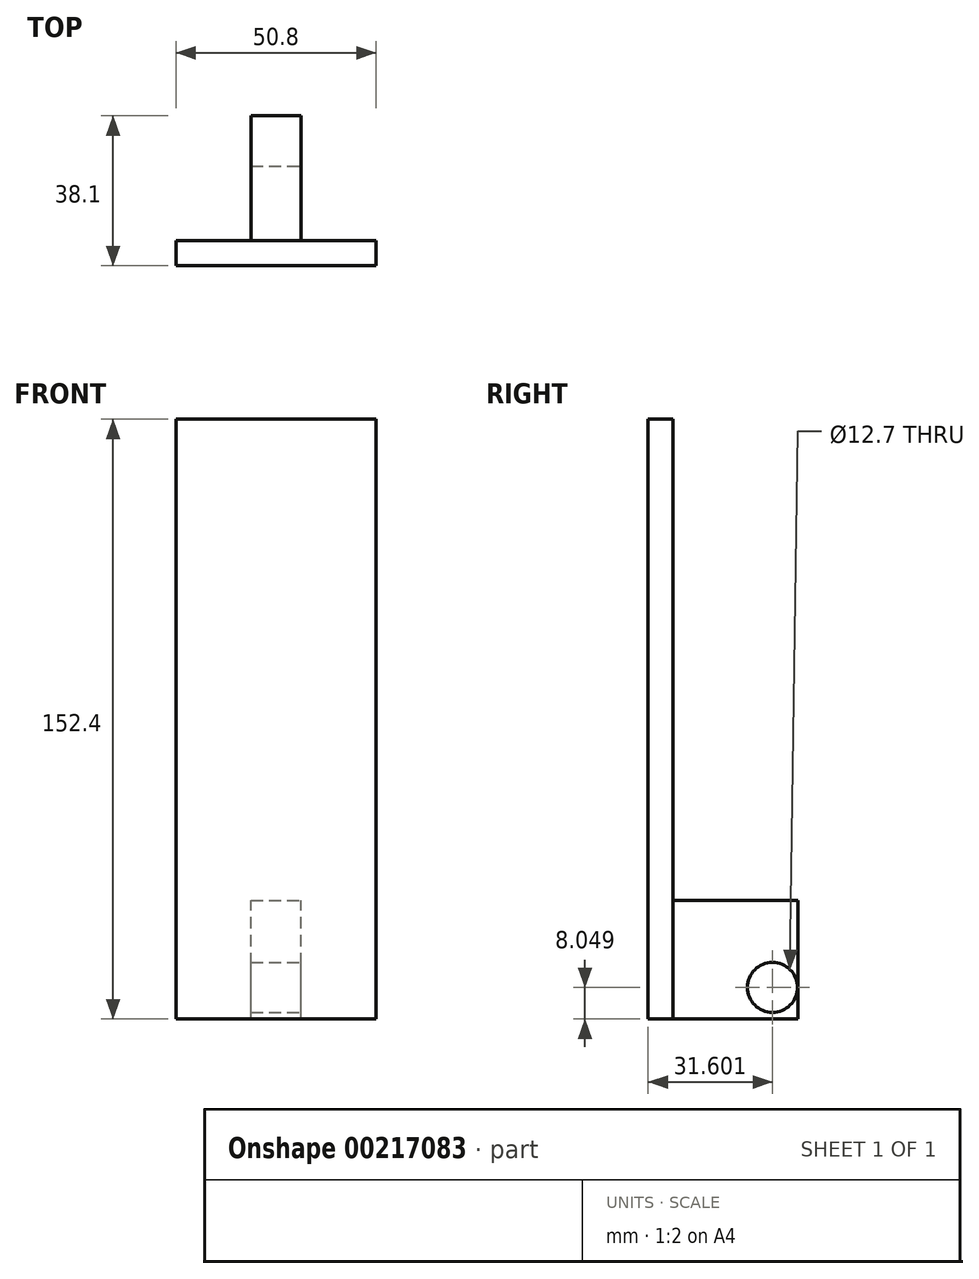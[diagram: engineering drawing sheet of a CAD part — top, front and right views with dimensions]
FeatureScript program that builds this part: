
annotation { "Feature Type Name" : "Feature", "Feature Type Description" : "" }
export const myFeature = defineFeature(function(context is Context, id is Id, definition is map)
    precondition{}
    {
        {
            var Q0;
            Q0=qCreatedBy(makeId("Front.planeOp"),FACE);
            var sketch = newSketch(context, id + "F0", { "sketchPlane" : qUnion([Q0])});
            skLineSegment(sketch, "E0.bottom", {"start": v(25.4, -76.2) * mm, "end": v(-25.4, -76.2) * mm});
            skLineSegment(sketch, "E0.top", {"start": v(25.4, 76.2) * mm, "end": v(-25.4, 76.2) * mm});
            skLineSegment(sketch, "E0.left", {"start": v(25.4, -76.2) * mm, "end": v(25.4, 76.2) * mm});
            skLineSegment(sketch, "E0.right", {"start": v(-25.4, -76.2) * mm, "end": v(-25.4, 76.2) * mm});
            skPoint(sketch, "E0.middle", {"position": v(0, 0) * mm});
            skSolve(sketch);
        }
        {
            var Q0;
            Q0=makeQuery(id+"F0.imprint","IMPRINT",FACE,{"disambiguationData":[TD([[makeQuery(id+"F0.imprint","IMPRINT",EDGE,{"derivedFrom":sQuery(id+"F0.wireOp",EDGE,"E0.bottom")}),-1.0]])]});
            extrude(context, id + "F1", {"entities" : qUnion([Q0]), "depth" : 6.35 * mm});
        }
        {
            var Q0;
            Q0=makeQuery(id+"F1.opExtrude","CAP_FACE",FACE,{"disambiguationData":[OSD([sQuery(id+"F0.wireOp",EDGE,"E0.bottom"),sQuery(id+"F0.wireOp",EDGE,"E0.top"),sQuery(id+"F0.wireOp",EDGE,"E0.left"),sQuery(id+"F0.wireOp",EDGE,"E0.right")])],"isStart":true});
            var sketch = newSketch(context, id + "F2", { "sketchPlane" : qUnion([Q0])});
            skLineSegment(sketch, "E1.bottom", {"start": v(6.35, -106.29) * mm, "end": v(-6.35, -106.29) * mm});
            skLineSegment(sketch, "E1.top", {"start": v(6.35, -46.11) * mm, "end": v(-6.35, -46.11) * mm});
            skLineSegment(sketch, "E1.left", {"start": v(6.35, -106.29) * mm, "end": v(6.35, -46.11) * mm});
            skLineSegment(sketch, "E1.right", {"start": v(-6.35, -106.29) * mm, "end": v(-6.35, -46.11) * mm});
            skPoint(sketch, "E1.middle", {"position": v(0, -76.2) * mm});
            skSolve(sketch);
        }
        {
            var Q0;
            {var subQ0=sQuery(id+"F2.wireOp",EDGE,"E1.top");Q0=makeQuery(id+"F2.imprint","IMPRINT",FACE,{"disambiguationData":[TD([[makeQuery(id+"F2.imprint","IMPRINT",EDGE,{"derivedFrom":subQ0}),1.0]])]});}
            extrude(context, id + "F3", {"entities" : qUnion([Q0]), "operationType" : NewBodyOperationType.ADD, "depth" : 31.75 * mm});
        }
        {
            var Q0;
            Q0=makeQuery(id+"F3.opExtrude","SWEPT_FACE",FACE,{"disambiguationData":[OSD([sQuery(id+"F2.wireOp",EDGE,"E1.right")])]});
            var sketch = newSketch(context, id + "F4", { "sketchPlane" : qUnion([Q0])});
            skCircle(sketch, "E2", {"center": v(25.4, -61.16) * mm, "radius": 6.35 * mm});
            skPoint(sketch, "E2.centerSnap0", {"position": v(31.75, -61.16) * mm});
            skSolve(sketch);
        }
        {
            var Q0;
            {var subQ0=sQuery(id+"F2.wireOp",EDGE,"E1.right");Q0=makeQuery(id+"F4.imprint","IMPRINT",FACE,{"disambiguationData":[TD([[makeQuery(id+"F4.imprint","IMPRINT",EDGE,{"derivedFrom":makeQuery(id+"F3.opExtrude","CAP_EDGE",EDGE,{"disambiguationData":[OSD([subQ0])],"isStart":false})}),1.0]])]});}
            var sketch = newSketch(context, id + "F5", { "sketchPlane" : qUnion([Q0])});
            skCircle(sketch, "E3", {"center": v(25.25, -68.15) * mm, "radius": 6.35 * mm});
            skSolve(sketch);
        }
        {
            var Q0;
            Q0=makeQuery(id+"F5.imprint","IMPRINT",FACE,{"disambiguationData":[TD([[makeQuery(id+"F5.imprint","IMPRINT",EDGE,{"derivedFrom":sQuery(id+"F5.wireOp",EDGE,"E3")}),1.0]])]});
            var Q1;
            Q1=sQuery(id+"F4.wireOp",EDGE,"E2");
            extrude(context, id + "F6", {"entities" : qUnion([Q0]), "operationType" : NewBodyOperationType.REMOVE, "surfaceEntities" : qUnion([Q1]), "endBound" : BoundingType.THROUGH_ALL, "oppositeDirection" : true, "depth" : 25.4 * mm});
        }
    });
